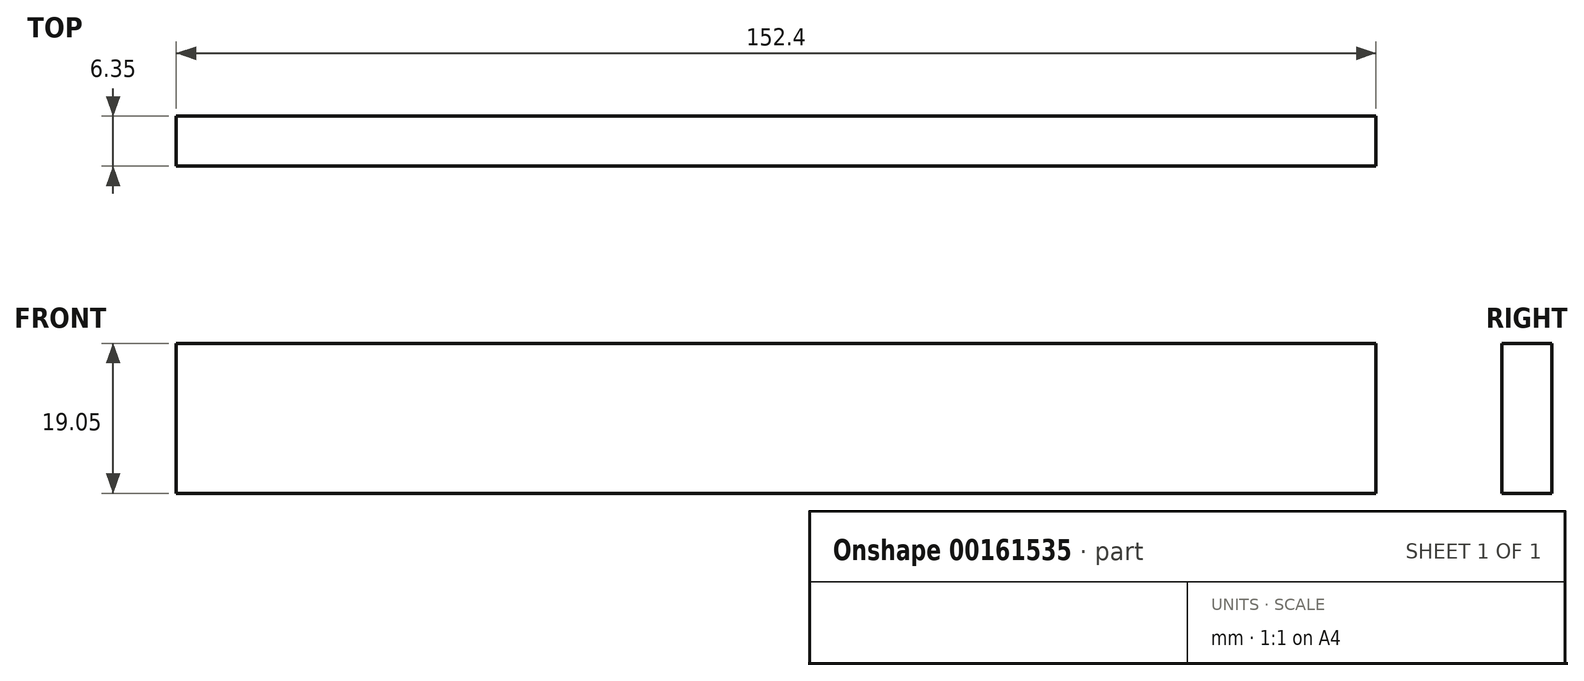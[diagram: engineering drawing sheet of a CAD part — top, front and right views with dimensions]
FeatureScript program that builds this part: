
annotation { "Feature Type Name" : "Feature", "Feature Type Description" : "" }
export const myFeature = defineFeature(function(context is Context, id is Id, definition is map)
    precondition{}
    {
        {
            var Q0;
            Q0=qCreatedBy(makeId("Front.planeOp"),FACE);
            var sketch = newSketch(context, id + "F0", { "sketchPlane" : qUnion([Q0])});
            skLineSegment(sketch, "E0.bottom", {"start": v(0, 0) * mm, "end": v(152.4, 0) * mm});
            skLineSegment(sketch, "E0.top", {"start": v(0, -19.05) * mm, "end": v(152.4, -19.05) * mm});
            skLineSegment(sketch, "E0.left", {"start": v(0, 0) * mm, "end": v(0, -19.05) * mm});
            skLineSegment(sketch, "E0.right", {"start": v(152.4, 0) * mm, "end": v(152.4, -19.05) * mm});
            skSolve(sketch);
        }
        {
            var Q0;
            Q0 = qSketchRegion(id + "F0", true);
            extrude(context, id + "F1", {"entities" : qUnion([Q0]), "depth" : 6.35 * mm});
        }
    });
